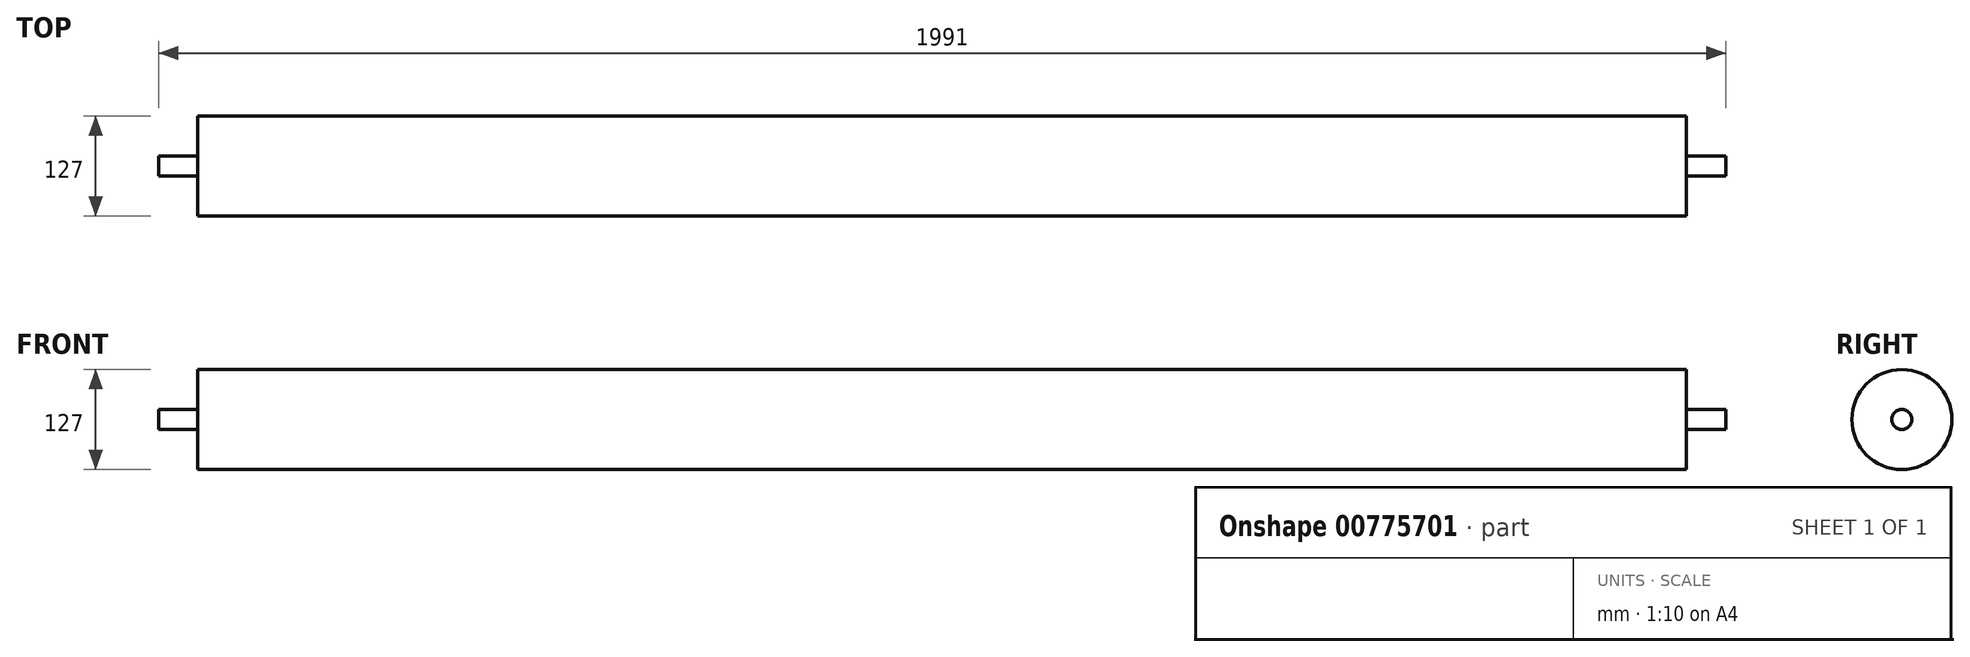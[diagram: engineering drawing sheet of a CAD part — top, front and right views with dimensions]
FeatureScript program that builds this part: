
annotation { "Feature Type Name" : "Feature", "Feature Type Description" : "" }
export const myFeature = defineFeature(function(context is Context, id is Id, definition is map)
    precondition{}
    {
        {
            var Q0;
            Q0=qCreatedBy(makeId("Front.planeOp"),FACE);
            var sketch = newSketch(context, id + "F0", { "sketchPlane" : qUnion([Q0])});
            skLineSegment(sketch, "E0", {"start": v(-991, 0) * mm, "end": v(1000, 0) * mm});
            skLineSegment(sketch, "E1", {"start": v(1000, 0) * mm, "end": v(1000, 12.7) * mm});
            skLineSegment(sketch, "E2", {"start": v(1000, 12.7) * mm, "end": v(950, 12.7) * mm});
            skLineSegment(sketch, "E3", {"start": v(950, 12.7) * mm, "end": v(950, 63.5) * mm});
            skLineSegment(sketch, "E4", {"start": v(950, 63.5) * mm, "end": v(-941, 63.5) * mm});
            skLineSegment(sketch, "E5", {"start": v(-941, 63.5) * mm, "end": v(-941, 12.7) * mm});
            skLineSegment(sketch, "E6", {"start": v(-941, 12.7) * mm, "end": v(-991, 12.7) * mm});
            skLineSegment(sketch, "E7", {"start": v(-991, 12.7) * mm, "end": v(-991, 0) * mm});
            skSolve(sketch);
        }
        {
            var Q0;
            Q0=makeQuery(id+"F0.imprint","IMPRINT",FACE,{"disambiguationData":[TD([[makeQuery(id+"F0.imprint","IMPRINT",EDGE,{"derivedFrom":sQuery(id+"F0.wireOp",EDGE,"E0")}),1.0]])]});
            var Q1;
            Q1=sQuery(id+"F0.wireOp",EDGE,"E0");
            revolve(context, id + "F1", {"surfaceOperationType" : NewSurfaceOperationType.NEW, "entities" : qUnion([Q0]), "axis" : qUnion([Q1]), "revolveType" : RevolveType.FULL});
        }
    });
